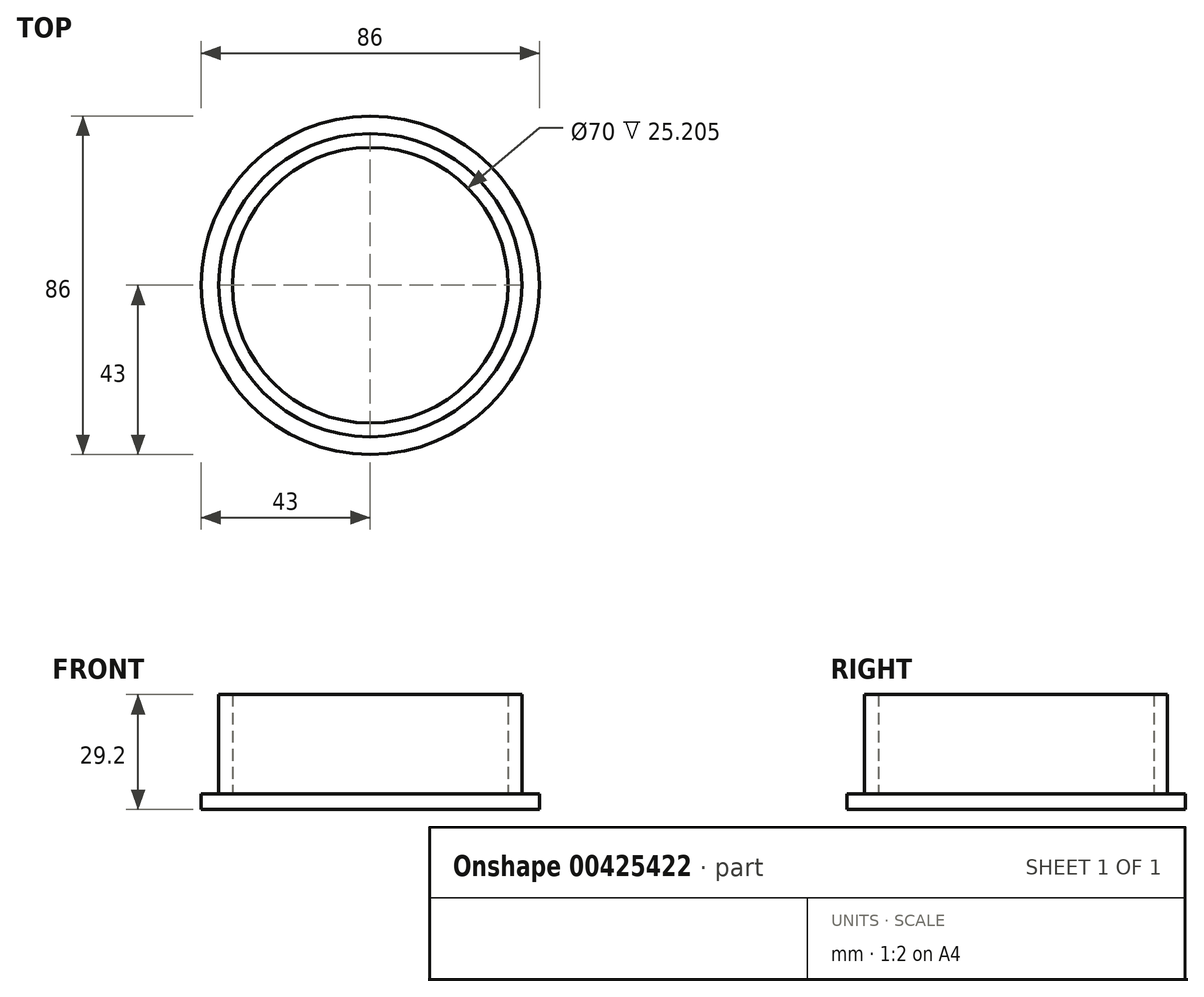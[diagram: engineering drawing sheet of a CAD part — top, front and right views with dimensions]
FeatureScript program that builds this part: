
annotation { "Feature Type Name" : "Feature", "Feature Type Description" : "" }
export const myFeature = defineFeature(function(context is Context, id is Id, definition is map)
    precondition{}
    {
        {
            var Q0;
            Q0=qCreatedBy(makeId("Front.planeOp"),FACE);
            var sketch = newSketch(context, id + "F0", { "sketchPlane" : qUnion([Q0])});
            skLineSegment(sketch, "E0.top", {"start": v(-35, -14.42) * mm, "end": v(-70, -14.42) * mm});
            skLineSegment(sketch, "E0.right", {"start": v(-70, -10.42) * mm, "end": v(-70, -14.42) * mm});
            skLineSegment(sketch, "E1.bottom", {"start": v(-70, -10.42) * mm, "end": v(-78, -10.42) * mm});
            skLineSegment(sketch, "E1.top", {"start": v(-70, -14.42) * mm, "end": v(-78, -14.42) * mm});
            skLineSegment(sketch, "E1.right", {"start": v(-78, -10.42) * mm, "end": v(-78, -14.42) * mm});
            skLineSegment(sketch, "E2.bottom", {"start": v(-70, -10.42) * mm, "end": v(-74, -10.42) * mm});
            skLineSegment(sketch, "E2.left", {"start": v(-70, -10.42) * mm, "end": v(-70, 14.78) * mm});
            skLineSegment(sketch, "E3.top", {"start": v(-74, -10.42) * mm, "end": v(-73.5, -10.42) * mm});
            skLineSegment(sketch, "E3.right", {"start": v(-73.5, 14.78) * mm, "end": v(-73.5, -10.42) * mm});
            skLineSegment(sketch, "E4", {"start": v(-73.5, 14.78) * mm, "end": v(-70, 14.78) * mm});
            skLineSegment(sketch, "E5.bottom", {"start": v(-70, -14.42) * mm, "end": v(-35, -14.42) * mm});
            skLineSegment(sketch, "E5.top", {"start": v(-70, -10.42) * mm, "end": v(-35, -10.42) * mm});
            skLineSegment(sketch, "E5.left", {"start": v(-70, -14.42) * mm, "end": v(-70, -10.42) * mm});
            skLineSegment(sketch, "E5.right", {"start": v(-35, -14.42) * mm, "end": v(-35, -10.42) * mm});
            skPoint(sketch, "E0.left.start.orphan", {"position": v(0, -10.42) * mm});
            skLineSegment(sketch, "E6.bottom", {"start": v(-35, -10.42) * mm, "end": v(-48.5, -10.42) * mm});
            skLineSegment(sketch, "E6.left", {"start": v(-35, -10.42) * mm, "end": v(-35, -14.42) * mm});
            skLineSegment(sketch, "E6.right", {"start": v(-48.5, -10.42) * mm, "end": v(-48.5, -14.42) * mm});
            skSolve(sketch);
        }
        {
            var Q0;
            Q0=makeQuery(id+"F0.imprint","IMPRINT",FACE,{"disambiguationData":[TD([[makeQuery(id+"F0.imprint","IMPRINT",EDGE,{"derivedFrom":sQuery(id+"F0.wireOp",EDGE,"0f115049-0156-4f6f-a15d-ce96dfcef0eb0.MirrorCS")}),-1.0]])]});
            var Q1;
            {var subQ2=sQuery(id+"F0.wireOp",EDGE,"E0.right");Q1=makeQuery(id+"F0.imprint","IMPRINT",FACE,{"disambiguationData":[TD([[makeQuery(id+"F0.imprint","IMPRINT",EDGE,{"derivedFrom":subQ2}),1.0]])]});}
            var Q2;
            Q2=makeQuery(id+"F0.imprint","IMPRINT",FACE,{"disambiguationData":[TD([[makeQuery(id+"F0.imprint","IMPRINT",EDGE,{"derivedFrom":sQuery(id+"F0.wireOp",EDGE,"ABhpSUum-iaYx-XLse-0V3W-c1DYquhyY7Ah.top")}),1.0]])]});
            var Q3;
            Q3=makeQuery(id+"F0.imprint","IMPRINT",FACE,{"disambiguationData":[TD([[makeQuery(id+"F0.imprint","IMPRINT",EDGE,{"derivedFrom":sQuery(id+"F0.wireOp",EDGE,"ABhpSUum-iaYx-XLse-0V3W-c1DYquhyY7Ah.top")}),-1.0]])]});
            var Q4;
            {var subQ11=sQuery(id+"F0.wireOp",EDGE,"L47Mw8el-83CS-MUxD-Dagk-7C3KnrcqyCCa.top");Q4=makeQuery(id+"F0.imprint","IMPRINT",FACE,{"disambiguationData":[TD([[makeQuery(id+"F0.imprint","IMPRINT",EDGE,{"derivedFrom":subQ11}),-1.0]])]});}
            var Q5;
            {var subQ2=sQuery(id+"F0.wireOp",EDGE,"E5.right");Q5=makeQuery(id+"F0.imprint","IMPRINT",FACE,{"disambiguationData":[TD([[makeQuery(id+"F0.imprint","IMPRINT",EDGE,{"derivedFrom":subQ2}),1.0]])]});}
            var Q6;
            {var subQ0=sQuery(id+"F0.wireOp",EDGE,"E2.left");Q6=makeQuery(id+"F0.imprint","IMPRINT",FACE,{"disambiguationData":[TD([[makeQuery(id+"F0.imprint","IMPRINT",EDGE,{"derivedFrom":subQ0}),1.0]])]});}
            var Q7;
            {var subQ4=sQuery(id+"F0.wireOp",EDGE,"L47Mw8el-83CS-MUxD-Dagk-7C3KnrcqyCCa.top");Q7=makeQuery(id+"F0.imprint","IMPRINT",FACE,{"disambiguationData":[TD([[makeQuery(id+"F0.imprint","IMPRINT",EDGE,{"derivedFrom":subQ4}),1.0]])]});}
            var Q8;
            {var subQ0=sQuery(id+"F0.wireOp",EDGE,"95BAVTFw-WXQf-HRlv-iQg9-a5IamtxKCCCA");Q8=makeQuery(id+"F0.imprint","IMPRINT",FACE,{"disambiguationData":[TD([[makeQuery(id+"F0.imprint","IMPRINT",EDGE,{"derivedFrom":subQ0}),-1.0]])]});}
            var Q9;
            {var subQ0=sQuery(id+"F0.wireOp",EDGE,"6470c43e-35dc-4b25-bab5-055d0ec69b560.MirrorCS");Q9=makeQuery(id+"F0.imprint","IMPRINT",FACE,{"disambiguationData":[TD([[makeQuery(id+"F0.imprint","IMPRINT",EDGE,{"derivedFrom":subQ0}),1.0]])]});}
            var Q10;
            {var subQ3=sQuery(id+"F0.wireOp",EDGE,"E0.right");Q10=makeQuery(id+"F0.imprint","IMPRINT",FACE,{"disambiguationData":[TD([[makeQuery(id+"F0.imprint","IMPRINT",EDGE,{"derivedFrom":subQ3}),-1.0]])]});}
            var Q11;
            Q11=makeQuery(id+"F0.imprint","IMPRINT",FACE,{"disambiguationData":[TD([[makeQuery(id+"F0.imprint","IMPRINT",EDGE,{"derivedFrom":sQuery(id+"F0.wireOp",EDGE,"0f115049-0156-4f6f-a15d-ce96dfcef0eb0.MirrorCS")}),1.0]])]});
            var Q12;
            Q12=sQuery(id+"F0.wireOp",EDGE,"E5.right");
            revolve(context, id + "F1", {"surfaceOperationType" : NewSurfaceOperationType.NEW, "entities" : qUnion([Q0, Q1, Q2, Q3, Q4, Q5, Q6, Q7, Q8, Q9, Q10, Q11]), "axis" : qUnion([Q12]), "revolveType" : RevolveType.FULL});
        }
    });
